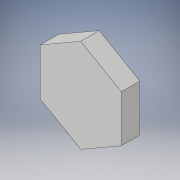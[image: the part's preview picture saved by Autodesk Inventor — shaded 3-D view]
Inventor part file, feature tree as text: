
AUTODESK INVENTOR PART (.ipt)
format: ipt  version: 2019 (Build 230136000, 136)  size: 97,280 bytes
history: native  units: mm
features: extrude x1, sketch x1
ambient origin geometry x8: Origin, YZ Plane, XZ Plane, XY Plane, X Axis, Y Axis, Z Axis, Center Point
bodies: Body1 (feature_tree)
feature tree (2):
  extrude  "Extrusion2"  Depth=40.0mm TaperAngle=0.0deg
  sketch  "Sketch2"  dims[d4=175.0mm d5=40.0mm d6=0.0mm]
